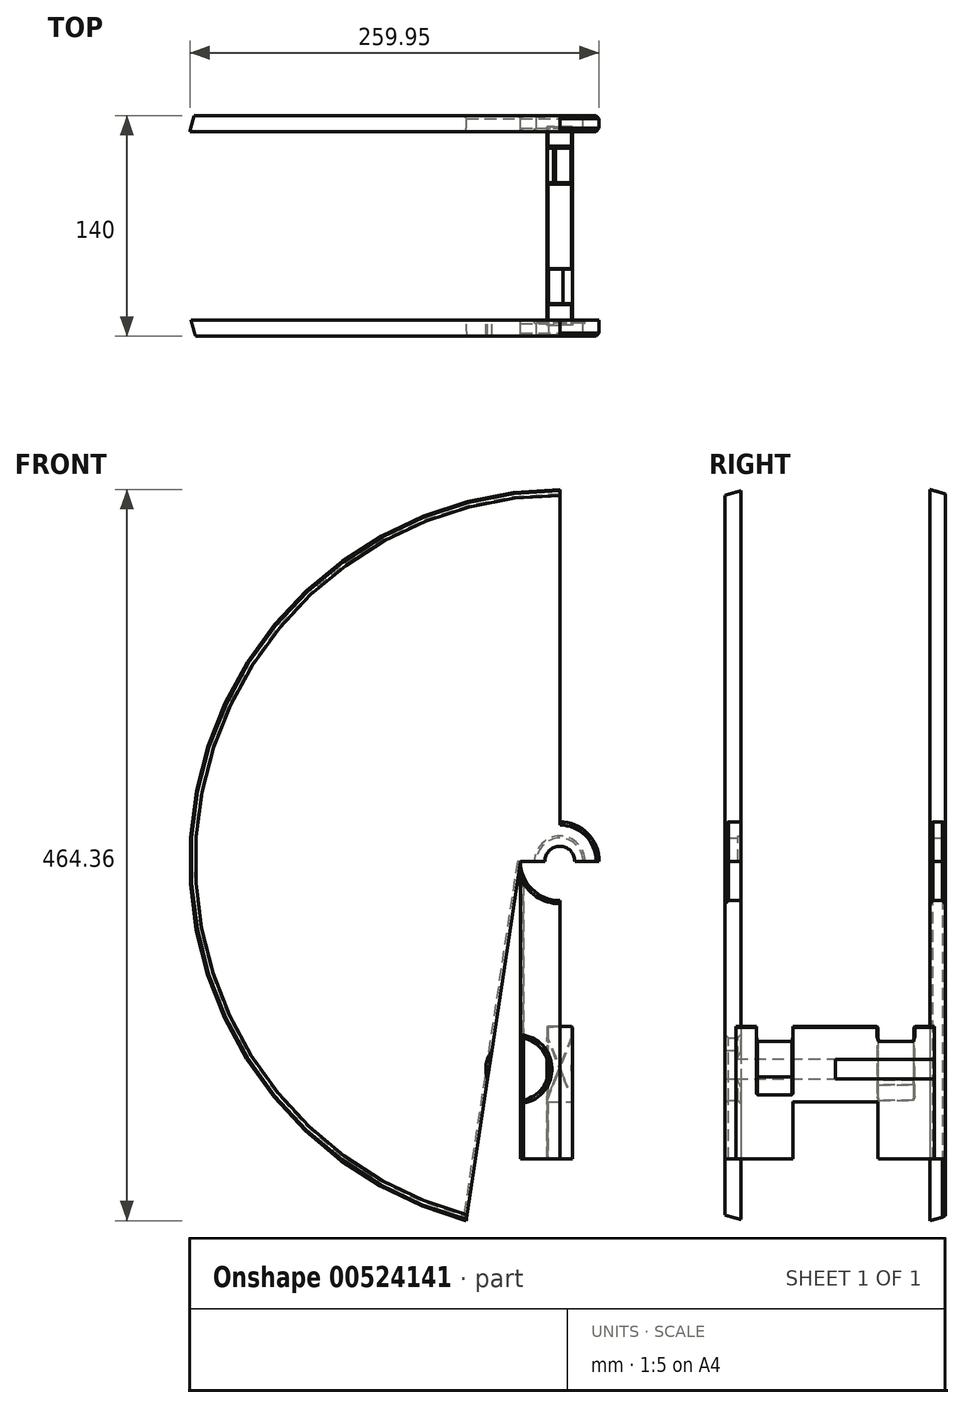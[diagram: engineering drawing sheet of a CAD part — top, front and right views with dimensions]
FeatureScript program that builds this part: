
annotation { "Feature Type Name" : "Feature", "Feature Type Description" : "" }
export const myFeature = defineFeature(function(context is Context, id is Id, definition is map)
    precondition{}
    {
        {
            var Q0;
            Q0=qCreatedBy(makeId("Right.planeOp"),FACE);
            var sketch = newSketch(context, id + "F0", { "sketchPlane" : qUnion([Q0])});
            skCircle(sketch, "E0", {"center": v(0, 0) * mm, "radius": 243.58 * mm});
            skLineSegment(sketch, "E1", {"start": v(1.44, 243.58) * mm, "end": v(1.44, -243.58) * mm});
            skCircle(sketch, "E2", {"center": v(0, 0) * mm, "radius": 251.5 * mm});
            skLineSegment(sketch, "E3", {"start": v(1.44, 243.58) * mm, "end": v(1.44, -357.35) * mm});
            skLineSegment(sketch, "E4", {"start": v(1.44, -357.35) * mm, "end": v(1.44, 517.62) * mm});
            skSolve(sketch);
        }
        {
            var Q0;
            Q0=qCreatedBy(makeId("Top.planeOp"),FACE);
            var sketch = newSketch(context, id + "F1", { "sketchPlane" : qUnion([Q0])});
            skCircle(sketch, "E5", {"center": v(0, 0) * mm, "radius": 243.58 * mm});
            skCircle(sketch, "E6", {"center": v(0, 0) * mm, "radius": 251.5 * mm});
            skSolve(sketch);
        }
        {
            var Q0;
            Q0=makeQuery(id+"F1.imprint","IMPRINT",FACE,{"disambiguationData":[TD([[makeQuery(id+"F1.imprint","IMPRINT",EDGE,{"derivedFrom":sQuery(id+"F1.wireOp",EDGE,"E5")}),1.0]])]});
            var sketch = newSketch(context, id + "F2", { "sketchPlane" : qUnion([Q0])});
            skCircle(sketch, "E7", {"center": v(0, 0) * mm, "radius": 50 * mm});
            skCircle(sketch, "E8", {"center": v(0, 0) * mm, "radius": 57.5 * mm});
            skSolve(sketch);
        }
        {
            var Q0;
            Q0=qCreatedBy(makeId("Front.planeOp"),FACE);
            var sketch = newSketch(context, id + "F3", { "sketchPlane" : qUnion([Q0])});
            skLineSegment(sketch, "E9.bottom", {"start": v(59.85, -25) * mm, "end": v(-59.85, -25) * mm});
            skLineSegment(sketch, "E9.top", {"start": v(59.85, 25) * mm, "end": v(-59.85, 25) * mm});
            skLineSegment(sketch, "E9.left", {"start": v(59.85, -25) * mm, "end": v(59.85, 25) * mm});
            skLineSegment(sketch, "E9.right", {"start": v(-59.85, -25) * mm, "end": v(-59.85, 25) * mm});
            skPoint(sketch, "E9.middle", {"position": v(0, 0) * mm});
            skCircle(sketch, "E10", {"center": v(0, 0) * mm, "radius": 14.75 * mm});
            skCircle(sketch, "E11", {"center": v(0, 0) * mm, "radius": 16 * mm});
            skCircle(sketch, "E12", {"center": v(0, 0) * mm, "radius": 9.5 * mm});
            skSolve(sketch);
        }
        {
            var Q0;
            Q0=qCreatedBy(makeId("Front.planeOp"),FACE);
            var sketch = newSketch(context, id + "F4", { "sketchPlane" : qUnion([Q0])});
            skCircle(sketch, "E13", {"center": v(0, 0) * mm, "radius": 25 * mm});
            skCircle(sketch, "E14", {"center": v(-1.44, -4.53) * mm, "radius": 243.58 * mm});
            skLineSegment(sketch, "E15", {"start": v(0, 239.04) * mm, "end": v(0, -248.1) * mm});
            skCircle(sketch, "E16", {"center": v(-1.44, -4.53) * mm, "radius": 251.5 * mm});
            skLineSegment(sketch, "E17", {"start": v(-25, 0) * mm, "end": v(-61.37, -240.62) * mm});
            skLineSegment(sketch, "E18.MirrorCS", {"start": v(25, 0) * mm, "end": v(61.37, -240.62) * mm});
            skLineSegment(sketch, "E19.bottom", {"start": v(-25, 0) * mm, "end": v(25, 0) * mm});
            skLineSegment(sketch, "E19.top", {"start": v(-25, -189.15) * mm, "end": v(25, -189.15) * mm});
            skLineSegment(sketch, "E19.left", {"start": v(-25, 0) * mm, "end": v(-25, -189.15) * mm});
            skLineSegment(sketch, "E19.right", {"start": v(25, 0) * mm, "end": v(25, -189.15) * mm});
            skSolve(sketch);
        }
        {
            var Q0;
            {var subQ0=sQuery(id+"F4.wireOp",EDGE,"E13");var subQ1=makeQuery(id+"F4.imprint","INTERSECT",VERTEX,{"derivedFrom":[subQ0,sQuery(id+"F4.wireOp",EDGE,"E17")]});Q0=makeQuery(id+"F4.imprint","IMPRINT",FACE,{"disambiguationData":[TD([[makeQuery(id+"F4.imprint","IMPRINT",EDGE,{"disambiguationData":[TD([[subQ1,1.0]])],"derivedFrom":subQ0}),1.0]])]});}
            var Q1;
            {var subQ0=sQuery(id+"F4.wireOp",EDGE,"E13");var subQ1=makeQuery(id+"F4.imprint","INTERSECT",VERTEX,{"derivedFrom":[subQ0,sQuery(id+"F4.wireOp",EDGE,"E18.MirrorCS")]});Q1=makeQuery(id+"F4.imprint","IMPRINT",FACE,{"disambiguationData":[TD([[makeQuery(id+"F4.imprint","IMPRINT",EDGE,{"disambiguationData":[TD([[subQ1,-1.0]])],"derivedFrom":subQ0}),1.0]])]});}
            var Q2;
            {var subQ0=sQuery(id+"F4.wireOp",EDGE,"E15");var subQ1=sQuery(id+"F4.wireOp",EDGE,"E13");var subQ2=makeQuery(id+"F4.imprint","INTERSECT",VERTEX,{"disambiguationData":[OD(1.0)],"derivedFrom":[subQ1,subQ0]});Q2=makeQuery(id+"F4.imprint","IMPRINT",FACE,{"disambiguationData":[TD([[makeQuery(id+"F4.imprint","IMPRINT",EDGE,{"disambiguationData":[TD([[subQ2,-1.0]])],"derivedFrom":subQ1}),-1.0]])]});}
            var Q3;
            {var subQ0=sQuery(id+"F4.wireOp",EDGE,"E19.left");Q3=makeQuery(id+"F4.imprint","IMPRINT",FACE,{"disambiguationData":[TD([[makeQuery(id+"F4.imprint","IMPRINT",EDGE,{"derivedFrom":subQ0}),1.0]])]});}
            var Q4;
            {var subQ0=sQuery(id+"F4.wireOp",EDGE,"E15");var subQ1=sQuery(id+"F4.wireOp",EDGE,"E13");var subQ2=makeQuery(id+"F4.imprint","INTERSECT",VERTEX,{"disambiguationData":[OD(1.0)],"derivedFrom":[subQ1,subQ0]});Q4=makeQuery(id+"F4.imprint","IMPRINT",FACE,{"disambiguationData":[TD([[makeQuery(id+"F4.imprint","IMPRINT",EDGE,{"disambiguationData":[TD([[subQ2,-1.0]])],"derivedFrom":subQ1}),1.0]])]});}
            var Q5;
            {var subQ1=sQuery(id+"F4.wireOp",EDGE,"E13");var subQ3=sQuery(id+"F4.wireOp",EDGE,"E15");var subQ4=makeQuery(id+"F4.imprint","INTERSECT",VERTEX,{"disambiguationData":[OD(1.0)],"derivedFrom":[subQ1,subQ3]});Q5=makeQuery(id+"F4.imprint","IMPRINT",FACE,{"disambiguationData":[TD([[makeQuery(id+"F4.imprint","IMPRINT",EDGE,{"disambiguationData":[TD([[subQ4,1.0]])],"derivedFrom":subQ3}),-1.0]])]});}
            extrude(context, id + "F5", {"entities" : qUnion([Q0, Q1, Q2, Q3, Q4, Q5]), "endBound" : BoundingType.SYMMETRIC, "depth" : 140 * mm, "hasSecondDirection" : true, "secondDirectionOppositeDirection" : true, "secondDirectionDepth" : 71 * mm});
        }
        {
            var Q0;
            {var subQ5=sQuery(id+"F4.wireOp",EDGE,"E13");var subQ6=makeQuery(id+"F4.imprint","INTERSECT",VERTEX,{"derivedFrom":[subQ5,sQuery(id+"F4.wireOp",EDGE,"E18.MirrorCS")]});Q0=makeQuery(id+"F4.imprint","IMPRINT",FACE,{"disambiguationData":[TD([[makeQuery(id+"F4.imprint","IMPRINT",EDGE,{"disambiguationData":[TD([[subQ6,-1.0]])],"derivedFrom":subQ5}),1.0]])]});}
            var Q1;
            {var subQ1=sQuery(id+"F4.wireOp",EDGE,"E13");var subQ3=sQuery(id+"F4.wireOp",EDGE,"E15");var subQ4=makeQuery(id+"F4.imprint","INTERSECT",VERTEX,{"disambiguationData":[OD(0.0)],"derivedFrom":[subQ1,subQ3]});Q1=makeQuery(id+"F4.imprint","IMPRINT",FACE,{"disambiguationData":[TD([[makeQuery(id+"F4.imprint","IMPRINT",EDGE,{"disambiguationData":[TD([[subQ4,-1.0]])],"derivedFrom":subQ3}),-1.0]])]});}
            var Q2;
            {var subQ1=sQuery(id+"F4.wireOp",EDGE,"E13");var subQ3=sQuery(id+"F4.wireOp",EDGE,"E15");var subQ4=makeQuery(id+"F4.imprint","INTERSECT",VERTEX,{"disambiguationData":[OD(1.0)],"derivedFrom":[subQ1,subQ3]});Q2=makeQuery(id+"F4.imprint","IMPRINT",FACE,{"disambiguationData":[TD([[makeQuery(id+"F4.imprint","IMPRINT",EDGE,{"disambiguationData":[TD([[subQ4,1.0]])],"derivedFrom":subQ3}),-1.0]])]});}
            var Q3;
            {var subQ0=sQuery(id+"F4.wireOp",EDGE,"E15");var subQ1=sQuery(id+"F4.wireOp",EDGE,"E13");var subQ2=makeQuery(id+"F4.imprint","INTERSECT",VERTEX,{"disambiguationData":[OD(1.0)],"derivedFrom":[subQ1,subQ0]});Q3=makeQuery(id+"F4.imprint","IMPRINT",FACE,{"disambiguationData":[TD([[makeQuery(id+"F4.imprint","IMPRINT",EDGE,{"disambiguationData":[TD([[subQ2,-1.0]])],"derivedFrom":subQ1}),1.0]])]});}
            var Q4;
            {var subQ0=sQuery(id+"F4.wireOp",EDGE,"E15");var subQ1=sQuery(id+"F4.wireOp",EDGE,"E13");var subQ2=makeQuery(id+"F4.imprint","INTERSECT",VERTEX,{"disambiguationData":[OD(1.0)],"derivedFrom":[subQ1,subQ0]});Q4=makeQuery(id+"F4.imprint","IMPRINT",FACE,{"disambiguationData":[TD([[makeQuery(id+"F4.imprint","IMPRINT",EDGE,{"disambiguationData":[TD([[subQ2,-1.0]])],"derivedFrom":subQ1}),-1.0]])]});}
            var Q5;
            {var subQ0=sQuery(id+"F4.wireOp",EDGE,"E19.left");Q5=makeQuery(id+"F4.imprint","IMPRINT",FACE,{"disambiguationData":[TD([[makeQuery(id+"F4.imprint","IMPRINT",EDGE,{"derivedFrom":subQ0}),1.0]])]});}
            extrude(context, id + "F6", {"entities" : qUnion([Q0, Q1, Q2, Q3, Q4, Q5]), "operationType" : NewBodyOperationType.REMOVE, "endBound" : BoundingType.SYMMETRIC, "oppositeDirection" : true, "depth" : 120 * mm});
        }
        {
            var Q0;
            {var subQ0=sQuery(id+"F0.wireOp",EDGE,"E4");var subQ1=sQuery(id+"F0.wireOp",EDGE,"E0");var subQ2=makeQuery(id+"F0.imprint","INTERSECT",VERTEX,{"disambiguationData":[OD(0.0)],"derivedFrom":[subQ1,subQ0]});Q0=makeQuery(id+"F0.imprint","IMPRINT",FACE,{"disambiguationData":[TD([[makeQuery(id+"F0.imprint","IMPRINT",EDGE,{"disambiguationData":[TD([[subQ2,1.0]])],"derivedFrom":subQ1}),1.0]])]});}
            var Q1;
            Q1=sQuery(id+"F0.wireOp",EDGE,"E4");
            revolve(context, id + "F7", {"operationType" : NewBodyOperationType.INTERSECT, "entities" : qUnion([Q0]), "axis" : qUnion([Q1]), "revolveType" : RevolveType.FULL});
        }
        {
            var Q0;
            Q0=makeQuery(id+"F3.imprint","IMPRINT",FACE,{"disambiguationData":[TD([[makeQuery(id+"F3.imprint","IMPRINT",EDGE,{"derivedFrom":sQuery(id+"F3.wireOp",EDGE,"E10")}),1.0]])]});
            var Q1;
            Q1=makeQuery(id+"F3.imprint","IMPRINT",FACE,{"disambiguationData":[TD([[makeQuery(id+"F3.imprint","IMPRINT",EDGE,{"derivedFrom":sQuery(id+"F3.wireOp",EDGE,"E10")}),-1.0]])]});
            var Q2;
            Q2=sQuery(id+"F4.wireOp",EDGE,"E13");
            extrude(context, id + "F8", {"entities" : qUnion([Q0, Q1]), "operationType" : NewBodyOperationType.REMOVE, "surfaceEntities" : qUnion([Q2]), "endBound" : BoundingType.SYMMETRIC, "depth" : 123.5 * mm});
        }
        {
            var Q0;
            Q0=makeQuery(id+"F3.imprint","IMPRINT",FACE,{"disambiguationData":[TD([[makeQuery(id+"F3.imprint","IMPRINT",EDGE,{"derivedFrom":sQuery(id+"F3.wireOp",EDGE,"E10")}),1.0]])]});
            extrude(context, id + "F9", {"entities" : qUnion([Q0]), "operationType" : NewBodyOperationType.REMOVE, "endBound" : BoundingType.SYMMETRIC, "depth" : 139 * mm});
        }
        {
            var Q0;
            Q0=qCreatedBy(makeId("Front.planeOp"),FACE);
            var sketch = newSketch(context, id + "F10", { "sketchPlane" : qUnion([Q0])});
            skLineSegment(sketch, "E20.bottom", {"start": v(-62.5, 105) * mm, "end": v(62.5, 105) * mm, "construction": true});
            skLineSegment(sketch, "E20.top", {"start": v(-62.5, -105) * mm, "end": v(62.5, -105) * mm, "construction": true});
            skLineSegment(sketch, "E20.left", {"start": v(-62.5, 105) * mm, "end": v(-62.5, -105) * mm, "construction": true});
            skLineSegment(sketch, "E20.right", {"start": v(62.5, 105) * mm, "end": v(62.5, -105) * mm, "construction": true});
            skPoint(sketch, "E20.middle", {"position": v(0, 0) * mm});
            skLineSegment(sketch, "E21", {"start": v(0, 0) * mm, "end": v(0, -232.3) * mm, "construction": true});
            skPoint(sketch, "E22.firstSnap0", {"position": v(0, -105) * mm});
            skLineSegment(sketch, "E22.bottom", {"start": v(0, -105) * mm, "end": v(-8.15, -105) * mm});
            skLineSegment(sketch, "E22.top", {"start": v(0, -232.3) * mm, "end": v(-8.15, -232.3) * mm});
            skLineSegment(sketch, "E22.left", {"start": v(0, -105) * mm, "end": v(0, -232.3) * mm});
            skLineSegment(sketch, "E22.right", {"start": v(-8.15, -105) * mm, "end": v(-8.15, -232.3) * mm});
            skLineSegment(sketch, "E23.bottom", {"start": v(0, -105) * mm, "end": v(8.15, -105) * mm});
            skLineSegment(sketch, "E23.top", {"start": v(0, -232.3) * mm, "end": v(8.15, -232.3) * mm});
            skLineSegment(sketch, "E23.right", {"start": v(8.15, -105) * mm, "end": v(8.15, -232.3) * mm});
            skSolve(sketch);
        }
        {
            var Q0;
            Q0=makeQuery(id+"F3.imprint","IMPRINT",FACE,{"disambiguationData":[TD([[makeQuery(id+"F3.imprint","IMPRINT",EDGE,{"derivedFrom":sQuery(id+"F3.wireOp",EDGE,"E12")}),1.0]])]});
            var Q1;
            Q1=sQuery(id+"F3.wireOp",EDGE,"E12");
            extrude(context, id + "F11", {"entities" : qUnion([Q0]), "operationType" : NewBodyOperationType.REMOVE, "surfaceEntities" : qUnion([Q1]), "endBound" : BoundingType.SYMMETRIC, "oppositeDirection" : true, "depth" : 200 * mm});
        }
        {
            var Q0;
            Q0=makeQuery(id+"F10.imprint","IMPRINT",FACE,{"disambiguationData":[TD([[makeQuery(id+"F10.imprint","IMPRINT",EDGE,{"derivedFrom":sQuery(id+"F10.wireOp",EDGE,"E23.bottom")}),-1.0]])]});
            var Q1;
            Q1=makeQuery(id+"F10.imprint","IMPRINT",FACE,{"disambiguationData":[TD([[makeQuery(id+"F10.imprint","IMPRINT",EDGE,{"derivedFrom":sQuery(id+"F10.wireOp",EDGE,"E22.bottom")}),1.0]])]});
            extrude(context, id + "F12", {"entities" : qUnion([Q0, Q1]), "operationType" : NewBodyOperationType.REMOVE, "endBound" : BoundingType.SYMMETRIC, "oppositeDirection" : true, "depth" : 126 * mm});
        }
        {
            var Q0;
            Q0=qCreatedBy(makeId("Front.planeOp"),FACE);
            var sketch = newSketch(context, id + "F13", { "sketchPlane" : qUnion([Q0])});
            skLineSegment(sketch, "E24.bottom", {"start": v(-62.5, 105) * mm, "end": v(62.5, 105) * mm, "construction": true});
            skLineSegment(sketch, "E24.top", {"start": v(-62.5, -105) * mm, "end": v(62.5, -105) * mm, "construction": true});
            skLineSegment(sketch, "E24.left", {"start": v(-62.5, 105) * mm, "end": v(-62.5, -105) * mm, "construction": true});
            skLineSegment(sketch, "E24.right", {"start": v(62.5, 105) * mm, "end": v(62.5, -105) * mm, "construction": true});
            skPoint(sketch, "E24.middle", {"position": v(0, 0) * mm});
            skLineSegment(sketch, "E25", {"start": v(0, 0) * mm, "end": v(0, -189) * mm, "construction": true});
            skPoint(sketch, "E26.firstSnap0", {"position": v(0, -105) * mm});
            skLineSegment(sketch, "E26.bottom", {"start": v(0, -105) * mm, "end": v(-8, -105) * mm});
            skLineSegment(sketch, "E26.top", {"start": v(0, -189) * mm, "end": v(-8, -189) * mm});
            skLineSegment(sketch, "E26.left", {"start": v(0, -105) * mm, "end": v(0, -189) * mm});
            skLineSegment(sketch, "E26.right", {"start": v(-8, -105) * mm, "end": v(-8, -189) * mm});
            skLineSegment(sketch, "E27.bottom", {"start": v(0, -105) * mm, "end": v(8, -105) * mm});
            skLineSegment(sketch, "E27.top", {"start": v(0, -189) * mm, "end": v(8, -189) * mm});
            skLineSegment(sketch, "E27.right", {"start": v(8, -105) * mm, "end": v(8, -189) * mm});
            skLineSegment(sketch, "E28", {"start": v(-63.01, -125.52) * mm, "end": v(62.14, -125.52) * mm, "construction": true});
            skLineSegment(sketch, "E29.bottom", {"start": v(-56.15, -105) * mm, "end": v(-48.17, -105) * mm});
            skSolve(sketch);
        }
        {
            var Q0;
            Q0=qCreatedBy(makeId("Front.planeOp"),FACE);
            var sketch = newSketch(context, id + "F14", { "sketchPlane" : qUnion([Q0])});
            skLineSegment(sketch, "E30", {"start": v(-75.64, -132) * mm, "end": v(82.36, -132) * mm, "construction": true});
            skCircle(sketch, "E31", {"center": v(-26.97, -132) * mm, "radius": 20 * mm});
            skCircle(sketch, "E32", {"center": v(27.03, -132) * mm, "radius": 20 * mm});
            skLineSegment(sketch, "E33", {"start": v(0, -132) * mm, "end": v(0, 0) * mm, "construction": true});
            skSolve(sketch);
        }
        {
            var Q0;
            Q0=makeQuery(id+"F13.imprint","IMPRINT",FACE,{"disambiguationData":[TD([[makeQuery(id+"F13.imprint","IMPRINT",EDGE,{"derivedFrom":sQuery(id+"F13.wireOp",EDGE,"E26.bottom")}),1.0]])]});
            var Q1;
            Q1=makeQuery(id+"F13.imprint","IMPRINT",FACE,{"disambiguationData":[TD([[makeQuery(id+"F13.imprint","IMPRINT",EDGE,{"derivedFrom":sQuery(id+"F13.wireOp",EDGE,"E27.bottom")}),-1.0]])]});
            extrude(context, id + "F15", {"entities" : qUnion([Q0, Q1]), "endBound" : BoundingType.SYMMETRIC, "depth" : 126 * mm});
        }
        {
            var Q0;
            Q0=makeQuery(id+"F14.imprint","IMPRINT",FACE,{"disambiguationData":[TD([[makeQuery(id+"F14.imprint","IMPRINT",EDGE,{"derivedFrom":sQuery(id+"F14.wireOp",EDGE,"E32")}),1.0]])]});
            extrude(context, id + "F16", {"entities" : qUnion([Q0]), "operationType" : NewBodyOperationType.REMOVE, "oppositeDirection" : true, "depth" : 125.4 * mm});
        }
        {
            var Q0;
            Q0=makeQuery(id+"F14.imprint","IMPRINT",FACE,{"disambiguationData":[TD([[makeQuery(id+"F14.imprint","IMPRINT",EDGE,{"derivedFrom":sQuery(id+"F14.wireOp",EDGE,"E31")}),1.0]])]});
            extrude(context, id + "F17", {"entities" : qUnion([Q0]), "operationType" : NewBodyOperationType.REMOVE, "depth" : 97.5 * mm});
        }
        {
            var Q0;
            Q0=qCreatedBy(makeId("Front.planeOp"),FACE);
            var sketch = newSketch(context, id + "F18", { "sketchPlane" : qUnion([Q0])});
            skCircle(sketch, "E34", {"center": v(0, 0) * mm, "radius": 242.5 * mm});
            skSolve(sketch);
        }
        {
            var Q0;
            Q0=makeQuery(id+"F14.imprint","IMPRINT",FACE,{"disambiguationData":[TD([[makeQuery(id+"F14.imprint","IMPRINT",EDGE,{"derivedFrom":sQuery(id+"F14.wireOp",EDGE,"E31")}),1.0]])]});
            extrude(context, id + "F19", {"entities" : qUnion([Q0]), "operationType" : NewBodyOperationType.REMOVE, "depth" : 159.82 * mm, "hasSecondDirection" : true, "secondDirectionOppositeDirection" : false, "secondDirectionDepth" : 5 * mm});
        }
        {
            var Q0;
            Q0=makeQuery(id+"F14.imprint","IMPRINT",FACE,{"disambiguationData":[TD([[makeQuery(id+"F14.imprint","IMPRINT",EDGE,{"derivedFrom":sQuery(id+"F14.wireOp",EDGE,"E32")}),1.0]])]});
            extrude(context, id + "F20", {"entities" : qUnion([Q0]), "operationType" : NewBodyOperationType.REMOVE, "oppositeDirection" : true, "depth" : 139.38 * mm, "hasSecondDirection" : true, "secondDirectionOppositeDirection" : true, "secondDirectionDepth" : 5 * mm});
        }
        {
            var Q0;
            Q0=qSketchRegion(id+"F14",true);
            var sketch = newSketch(context, id + "F21", { "sketchPlane" : qUnion([Q0])});
            skLineSegment(sketch, "E35", {"start": v(-64.6, -131.33) * mm, "end": v(93.4, -131.33) * mm, "construction": true});
            skCircle(sketch, "E36", {"center": v(-26.64, -131.33) * mm, "radius": 25 * mm});
            skCircle(sketch, "E37", {"center": v(26.36, -131.33) * mm, "radius": 25 * mm});
            skLineSegment(sketch, "E38", {"start": v(0, -131.33) * mm, "end": v(0, 0.67) * mm, "construction": true});
            skSolve(sketch);
        }
        {
            var Q0;
            Q0=qSketchRegion(id+"F21",true);
            var sketch = newSketch(context, id + "F22", { "sketchPlane" : qUnion([Q0])});
            skLineSegment(sketch, "E39.bottom", {"start": v(-20, -81.91) * mm, "end": v(20, -81.91) * mm});
            skLineSegment(sketch, "E39.top", {"start": v(-20, -181.91) * mm, "end": v(20, -181.91) * mm});
            skLineSegment(sketch, "E39.left", {"start": v(-20, -81.91) * mm, "end": v(-20, -181.91) * mm});
            skLineSegment(sketch, "E39.right", {"start": v(20, -81.91) * mm, "end": v(20, -181.91) * mm});
            skPoint(sketch, "E39.middle", {"position": v(0, -131.91) * mm});
            skLineSegment(sketch, "E40", {"start": v(20, -181.91) * mm, "end": v(-20, -81.91) * mm});
            skLineSegment(sketch, "E41", {"start": v(20, -81.91) * mm, "end": v(-20, -181.91) * mm});
            skSolve(sketch);
        }
        {
            var Q0;
            {var subQ0=sQuery(id+"F22.wireOp",EDGE,"E39.left");var subQ1=makeQuery(id+"F21.imprint","IMPRINT",EDGE,{"derivedFrom":sQuery(id+"F21.wireOp",EDGE,"E36")});var subQ2=makeQuery(id+"F22.imprint","INTERSECT",VERTEX,{"disambiguationData":[OD(0.0)],"derivedFrom":[subQ1,subQ0]});Q0=makeQuery(id+"F22.imprint","IMPRINT",FACE,{"disambiguationData":[TD([[makeQuery(id+"F22.imprint","IMPRINT",EDGE,{"disambiguationData":[TD([[subQ2,-1.0]])],"derivedFrom":subQ0}),-1.0]])]});}
            var Q1;
            Q1=makeQuery(id+"F21.imprint","IMPRINT",FACE,{"disambiguationData":[TD([[makeQuery(id+"F21.imprint","IMPRINT",EDGE,{"derivedFrom":sQuery(id+"F21.wireOp",EDGE,"E36")}),1.0]])]});
            var Q2;
            Q2=makeQuery(id+"F21.imprint","IMPRINT",FACE,{"disambiguationData":[TD([[makeQuery(id+"F21.imprint","IMPRINT",EDGE,{"derivedFrom":makeQuery(id+"F14.imprint","IMPRINT",EDGE,{"derivedFrom":sQuery(id+"F14.wireOp",EDGE,"E31")})}),1.0]])]});
            var Q3;
            {var subQ1=sQuery(id+"F22.wireOp",EDGE,"E39.left");var subQ3=makeQuery(id+"F21.imprint","IMPRINT",EDGE,{"derivedFrom":sQuery(id+"F21.wireOp",EDGE,"E36")});var subQ4=makeQuery(id+"F22.imprint","INTERSECT",VERTEX,{"disambiguationData":[OD(0.0)],"derivedFrom":[subQ3,subQ1]});Q3=makeQuery(id+"F22.imprint","IMPRINT",FACE,{"disambiguationData":[TD([[makeQuery(id+"F22.imprint","IMPRINT",EDGE,{"disambiguationData":[TD([[subQ4,1.0]])],"derivedFrom":subQ3}),-1.0]])]});}
            var Q4;
            {var subQ1=sQuery(id+"F22.wireOp",EDGE,"E39.bottom");Q4=makeQuery(id+"F22.imprint","IMPRINT",FACE,{"disambiguationData":[TD([[makeQuery(id+"F22.imprint","IMPRINT",EDGE,{"derivedFrom":subQ1}),-1.0]])]});}
            var Q5;
            {var subQ0=sQuery(id+"F22.wireOp",EDGE,"E41");var subQ1=sQuery(id+"F22.wireOp",EDGE,"E40");var subQ2=makeQuery(id+"F22.imprint","INTERSECT",VERTEX,{"derivedFrom":[subQ1,subQ0]});Q5=makeQuery(id+"F22.imprint","IMPRINT",FACE,{"disambiguationData":[TD([[makeQuery(id+"F22.imprint","IMPRINT",EDGE,{"disambiguationData":[TD([[subQ2,-1.0]])],"derivedFrom":subQ1}),1.0]])]});}
            var Q6;
            {var subQ0=sQuery(id+"F22.wireOp",EDGE,"E41");var subQ1=makeQuery(id+"F21.imprint","IMPRINT",EDGE,{"derivedFrom":sQuery(id+"F21.wireOp",EDGE,"E37")});var subQ2=makeQuery(id+"F22.imprint","INTERSECT",VERTEX,{"disambiguationData":[OD(0.0)],"derivedFrom":[subQ1,subQ0]});Q6=makeQuery(id+"F22.imprint","IMPRINT",FACE,{"disambiguationData":[TD([[makeQuery(id+"F22.imprint","IMPRINT",EDGE,{"disambiguationData":[TD([[subQ2,-1.0]])],"derivedFrom":subQ0}),-1.0]])]});}
            extrude(context, id + "F23", {"entities" : qUnion([Q0, Q1, Q2, Q3, Q4, Q5, Q6]), "operationType" : NewBodyOperationType.REMOVE, "oppositeDirection" : true, "depth" : 50 * mm, "hasSecondDirection" : true, "secondDirectionOppositeDirection" : true, "secondDirectionDepth" : 27 * mm});
        }
        {
            var Q0;
            {var subQ0=sQuery(id+"F22.wireOp",EDGE,"E39.right");var subQ1=makeQuery(id+"F21.imprint","IMPRINT",EDGE,{"derivedFrom":makeQuery(id+"F14.imprint","IMPRINT",EDGE,{"derivedFrom":sQuery(id+"F14.wireOp",EDGE,"E32")})});var subQ2=makeQuery(id+"F22.imprint","INTERSECT",VERTEX,{"disambiguationData":[OD(0.0)],"derivedFrom":[subQ1,subQ0]});Q0=makeQuery(id+"F22.imprint","IMPRINT",FACE,{"disambiguationData":[TD([[makeQuery(id+"F22.imprint","IMPRINT",EDGE,{"disambiguationData":[TD([[subQ2,-1.0]])],"derivedFrom":subQ0}),-1.0]])]});}
            var Q1;
            {var subQ1=makeQuery(id+"F21.imprint","IMPRINT",EDGE,{"derivedFrom":sQuery(id+"F21.wireOp",EDGE,"E37")});var subQ4=sQuery(id+"F22.wireOp",EDGE,"E39.right");var subQ5=makeQuery(id+"F22.imprint","INTERSECT",VERTEX,{"disambiguationData":[OD(0.0)],"derivedFrom":[subQ1,subQ4]});Q1=makeQuery(id+"F22.imprint","IMPRINT",FACE,{"disambiguationData":[TD([[makeQuery(id+"F22.imprint","IMPRINT",EDGE,{"disambiguationData":[TD([[subQ5,-1.0]])],"derivedFrom":subQ4}),-1.0]])]});}
            var Q2;
            Q2=makeQuery(id+"F21.imprint","IMPRINT",FACE,{"disambiguationData":[TD([[makeQuery(id+"F21.imprint","IMPRINT",EDGE,{"derivedFrom":makeQuery(id+"F14.imprint","IMPRINT",EDGE,{"derivedFrom":sQuery(id+"F14.wireOp",EDGE,"E32")})}),1.0]])]});
            var Q3;
            {var subQ0=sQuery(id+"F22.wireOp",EDGE,"E41");var subQ1=sQuery(id+"F22.wireOp",EDGE,"E40");var subQ2=makeQuery(id+"F22.imprint","INTERSECT",VERTEX,{"derivedFrom":[subQ1,subQ0]});Q3=makeQuery(id+"F22.imprint","IMPRINT",FACE,{"disambiguationData":[TD([[makeQuery(id+"F22.imprint","IMPRINT",EDGE,{"disambiguationData":[TD([[subQ2,1.0]])],"derivedFrom":subQ1}),-1.0]])]});}
            var Q4;
            {var subQ1=sQuery(id+"F22.wireOp",EDGE,"E39.right");var subQ3=makeQuery(id+"F21.imprint","IMPRINT",EDGE,{"derivedFrom":sQuery(id+"F21.wireOp",EDGE,"E37")});var subQ4=makeQuery(id+"F22.imprint","INTERSECT",VERTEX,{"disambiguationData":[OD(0.0)],"derivedFrom":[subQ3,subQ1]});Q4=makeQuery(id+"F22.imprint","IMPRINT",FACE,{"disambiguationData":[TD([[makeQuery(id+"F22.imprint","IMPRINT",EDGE,{"disambiguationData":[TD([[subQ4,-1.0]])],"derivedFrom":subQ3}),-1.0]])]});}
            var Q5;
            {var subQ1=sQuery(id+"F22.wireOp",EDGE,"E39.bottom");Q5=makeQuery(id+"F22.imprint","IMPRINT",FACE,{"disambiguationData":[TD([[makeQuery(id+"F22.imprint","IMPRINT",EDGE,{"derivedFrom":subQ1}),-1.0]])]});}
            var Q6;
            Q6=makeQuery(id+"F21.imprint","IMPRINT",FACE,{"disambiguationData":[TD([[makeQuery(id+"F21.imprint","IMPRINT",EDGE,{"derivedFrom":sQuery(id+"F21.wireOp",EDGE,"E37")}),1.0]])]});
            var Q7;
            {var subQ0=sQuery(id+"F22.wireOp",EDGE,"E40");var subQ1=makeQuery(id+"F21.imprint","IMPRINT",EDGE,{"derivedFrom":sQuery(id+"F21.wireOp",EDGE,"E36")});var subQ2=makeQuery(id+"F22.imprint","INTERSECT",VERTEX,{"disambiguationData":[OD(0.0)],"derivedFrom":[subQ1,subQ0]});Q7=makeQuery(id+"F22.imprint","IMPRINT",FACE,{"disambiguationData":[TD([[makeQuery(id+"F22.imprint","IMPRINT",EDGE,{"disambiguationData":[TD([[subQ2,-1.0]])],"derivedFrom":subQ0}),-1.0]])]});}
            extrude(context, id + "F24", {"entities" : qUnion([Q0, Q1, Q2, Q3, Q4, Q5, Q6, Q7]), "operationType" : NewBodyOperationType.REMOVE, "depth" : 50 * mm, "hasSecondDirection" : true, "secondDirectionOppositeDirection" : false, "secondDirectionDepth" : 27 * mm});
        }
        {
            var Q0;
            Q0=makeQuery(id+"F5.opExtrude","CAP_EDGE",EDGE,{"disambiguationData":[OSD([sQuery(id+"F4.wireOp",EDGE,"E17")])],"isStart":true});
            var Q1;
            Q1=makeQuery(id+"F5.opExtrude","CAP_EDGE",EDGE,{"disambiguationData":[OSD([sQuery(id+"F4.wireOp",EDGE,"E18.MirrorCS")])],"isStart":true});
            var Q2;
            Q2=makeQuery(id+"F5.opExtrude","CAP_EDGE",EDGE,{"disambiguationData":[OSD([sQuery(id+"F4.wireOp",EDGE,"E19.right")])],"isStart":false});
            var Q3;
            Q3=makeQuery(id+"F5.opExtrude","CAP_EDGE",EDGE,{"disambiguationData":[OSD([sQuery(id+"F4.wireOp",EDGE,"E13")])],"isStart":false});
            var Q4;
            Q4=makeQuery(id+"F5.opExtrude","CAP_EDGE",EDGE,{"disambiguationData":[OSD([sQuery(id+"F4.wireOp",EDGE,"E13")])],"isStart":true});
            var Q5;
            Q5=makeQuery(id+"F5.opExtrude","CAP_EDGE",EDGE,{"disambiguationData":[OSD([sQuery(id+"F4.wireOp",EDGE,"E19.left")])],"isStart":true});
            var Q6;
            Q6=makeQuery(id+"F5.opExtrude","CAP_EDGE",EDGE,{"disambiguationData":[OSD([sQuery(id+"F4.wireOp",EDGE,"E19.right")])],"isStart":true});
            var Q7;
            Q7=makeQuery(id+"F17.boolean.opBoolean","INTERSECT",EDGE,{"derivedFrom":[makeQuery(id+"F5.opExtrude","CAP_FACE",FACE,{"disambiguationData":[OSD([sQuery(id+"F4.wireOp",EDGE,"E13"),sQuery(id+"F4.wireOp",EDGE,"E19.top"),sQuery(id+"F4.wireOp",EDGE,"E19.left"),sQuery(id+"F4.wireOp",EDGE,"E19.right")])],"isStart":false}),makeQuery(id+"F17.opExtrude","SWEPT_FACE",FACE,{"disambiguationData":[OSD([sQuery(id+"F14.wireOp",EDGE,"E31")])]})]});
            var Q8;
            Q8=makeQuery(id+"F16.boolean.opBoolean","INTERSECT",EDGE,{"derivedFrom":[makeQuery(id+"F5.opExtrude","CAP_FACE",FACE,{"disambiguationData":[OSD([sQuery(id+"F4.wireOp",EDGE,"E13"),sQuery(id+"F4.wireOp",EDGE,"E19.top"),sQuery(id+"F4.wireOp",EDGE,"E19.left"),sQuery(id+"F4.wireOp",EDGE,"E19.right")])],"isStart":true}),makeQuery(id+"F16.opExtrude","SWEPT_FACE",FACE,{"disambiguationData":[OSD([sQuery(id+"F14.wireOp",EDGE,"E32")])]})]});
            var Q9;
            {var subQ0=sQuery(id+"F4.wireOp",EDGE,"E19.left");var subQ1=sQuery(id+"F4.wireOp",EDGE,"E19.top");Q9=makeQuery(id+"F17.boolean.opBoolean","SPLIT",EDGE,{"disambiguationData":[TD([makeQuery(id+"F5.opExtrude","SWEPT_FACE",FACE,{"disambiguationData":[OSD([subQ1])]})])],"derivedFrom":makeQuery(id+"F5.opExtrude","CAP_EDGE",EDGE,{"disambiguationData":[OSD([subQ0])],"isStart":false})});}
            var Q10;
            Q10=makeQuery(id+"F6.boolean.opBoolean","COPY",EDGE,{"derivedFrom":makeQuery(id+"F6.opExtrude","CAP_EDGE",EDGE,{"disambiguationData":[OSD([sQuery(id+"F4.wireOp",EDGE,"E19.right")])],"isStart":true})});
            var Q11;
            Q11=makeQuery(id+"F6.boolean.opBoolean","COPY",EDGE,{"derivedFrom":makeQuery(id+"F6.opExtrude","CAP_EDGE",EDGE,{"disambiguationData":[OSD([sQuery(id+"F4.wireOp",EDGE,"E13")])],"isStart":true})});
            var Q12;
            Q12=makeQuery(id+"F6.boolean.opBoolean","COPY",EDGE,{"derivedFrom":makeQuery(id+"F6.opExtrude","CAP_EDGE",EDGE,{"disambiguationData":[OSD([sQuery(id+"F4.wireOp",EDGE,"E19.left")])],"isStart":false})});
            var Q13;
            Q13=makeQuery(id+"F6.boolean.opBoolean","COPY",EDGE,{"derivedFrom":makeQuery(id+"F6.opExtrude","CAP_EDGE",EDGE,{"disambiguationData":[OSD([sQuery(id+"F4.wireOp",EDGE,"E13")])],"isStart":false})});
            var Q14;
            {var subQ0=sQuery(id+"F4.wireOp",EDGE,"E13");var subQ1=sQuery(id+"F4.wireOp",EDGE,"E19.right");Q14=makeQuery(id+"F16.boolean.opBoolean","SPLIT",EDGE,{"disambiguationData":[TD([makeQuery(id+"F5.opExtrude","SWEPT_FACE",FACE,{"disambiguationData":[OSD([subQ0])]})])],"derivedFrom":makeQuery(id+"F6.boolean.opBoolean","COPY",EDGE,{"derivedFrom":makeQuery(id+"F6.opExtrude","CAP_EDGE",EDGE,{"disambiguationData":[OSD([subQ1])],"isStart":false})})});}
            var Q15;
            {var subQ0=sQuery(id+"F4.wireOp",EDGE,"E19.top");var subQ1=sQuery(id+"F4.wireOp",EDGE,"E19.right");Q15=makeQuery(id+"F16.boolean.opBoolean","SPLIT",EDGE,{"disambiguationData":[TD([makeQuery(id+"F5.opExtrude","SWEPT_FACE",FACE,{"disambiguationData":[OSD([subQ0])]})])],"derivedFrom":makeQuery(id+"F6.boolean.opBoolean","COPY",EDGE,{"derivedFrom":makeQuery(id+"F6.opExtrude","CAP_EDGE",EDGE,{"disambiguationData":[OSD([subQ1])],"isStart":false})})});}
            var Q16;
            {var subQ0=sQuery(id+"F4.wireOp",EDGE,"E19.left");var subQ1=sQuery(id+"F4.wireOp",EDGE,"E19.top");var subQ2=sQuery(id+"F4.wireOp",EDGE,"E19.right");var subQ3=sQuery(id+"F4.wireOp",EDGE,"E13");Q16=makeQuery(id+"F16.boolean.opBoolean","INTERSECT",EDGE,{"disambiguationData":[OD(1.0)],"derivedFrom":[makeQuery(id+"F8.boolean.opBoolean","SPLIT",FACE,{"disambiguationData":[TD([makeQuery(id+"F5.opExtrude","SWEPT_FACE",FACE,{"disambiguationData":[OSD([subQ3])]})])],"derivedFrom":makeQuery(id+"F6.boolean.opBoolean","COPY",FACE,{"derivedFrom":makeQuery(id+"F6.opExtrude","CAP_FACE",FACE,{"disambiguationData":[OSD([subQ3,subQ1,subQ0,subQ2])],"isStart":false})})}),makeQuery(id+"F16.opExtrude","SWEPT_FACE",FACE,{"disambiguationData":[OSD([sQuery(id+"F14.wireOp",EDGE,"E32")])]})]});}
            var Q17;
            {var subQ0=sQuery(id+"F4.wireOp",EDGE,"E19.left");var subQ1=sQuery(id+"F4.wireOp",EDGE,"E19.top");var subQ2=sQuery(id+"F4.wireOp",EDGE,"E19.right");var subQ3=sQuery(id+"F4.wireOp",EDGE,"E13");Q17=makeQuery(id+"F16.boolean.opBoolean","INTERSECT",EDGE,{"disambiguationData":[OD(0.0)],"derivedFrom":[makeQuery(id+"F8.boolean.opBoolean","SPLIT",FACE,{"disambiguationData":[TD([makeQuery(id+"F5.opExtrude","SWEPT_FACE",FACE,{"disambiguationData":[OSD([subQ3])]})])],"derivedFrom":makeQuery(id+"F6.boolean.opBoolean","COPY",FACE,{"derivedFrom":makeQuery(id+"F6.opExtrude","CAP_FACE",FACE,{"disambiguationData":[OSD([subQ3,subQ1,subQ0,subQ2])],"isStart":false})})}),makeQuery(id+"F16.opExtrude","SWEPT_FACE",FACE,{"disambiguationData":[OSD([sQuery(id+"F14.wireOp",EDGE,"E32")])]})]});}
            var Q18;
            Q18=makeQuery(id+"F16.boolean.opBoolean","INTERSECT",EDGE,{"derivedFrom":[makeQuery(id+"F12.boolean.opBoolean","COPY",FACE,{"derivedFrom":makeQuery(id+"F12.opExtrude","CAP_FACE",FACE,{"disambiguationData":[OSD([sQuery(id+"F10.wireOp",EDGE,"E22.bottom"),sQuery(id+"F10.wireOp",EDGE,"E22.top"),sQuery(id+"F10.wireOp",EDGE,"E22.right"),sQuery(id+"F10.wireOp",EDGE,"E23.bottom"),sQuery(id+"F10.wireOp",EDGE,"E23.top"),sQuery(id+"F10.wireOp",EDGE,"E23.right")])],"isStart":false})}),makeQuery(id+"F16.opExtrude","SWEPT_FACE",FACE,{"disambiguationData":[OSD([sQuery(id+"F14.wireOp",EDGE,"E32")])]})]});
            var Q19;
            Q19=makeQuery(id+"F20.boolean.opBoolean","INTERSECT",EDGE,{"derivedFrom":[makeQuery(id+"F15.opExtrude","SWEPT_FACE",FACE,{"disambiguationData":[OSD([sQuery(id+"F13.wireOp",EDGE,"E27.right")])]}),makeQuery(id+"F20.opExtrude","CAP_FACE",FACE,{"disambiguationData":[OSD([sQuery(id+"F14.wireOp",EDGE,"E32")])],"isStart":true})]});
            var Q20;
            Q20=makeQuery(id+"F19.boolean.opBoolean","COPY",EDGE,{"derivedFrom":makeQuery(id+"F19.opExtrude","CAP_EDGE",EDGE,{"disambiguationData":[OSD([sQuery(id+"F14.wireOp",EDGE,"E31")])],"isStart":true})});
            var Q21;
            Q21=makeQuery(id+"F19.boolean.opBoolean","INTERSECT",EDGE,{"derivedFrom":[makeQuery(id+"F15.opExtrude","CAP_FACE",FACE,{"disambiguationData":[OSD([sQuery(id+"F13.wireOp",EDGE,"E26.bottom"),sQuery(id+"F13.wireOp",EDGE,"E26.top"),sQuery(id+"F13.wireOp",EDGE,"E26.right"),sQuery(id+"F13.wireOp",EDGE,"E27.bottom"),sQuery(id+"F13.wireOp",EDGE,"E27.top"),sQuery(id+"F13.wireOp",EDGE,"E27.right")])],"isStart":false}),makeQuery(id+"F19.opExtrude","SWEPT_FACE",FACE,{"disambiguationData":[OSD([sQuery(id+"F14.wireOp",EDGE,"E31")])]})]});
            var Q22;
            {var subQ0=sQuery(id+"F4.wireOp",EDGE,"E19.left");var subQ1=sQuery(id+"F4.wireOp",EDGE,"E19.top");var subQ2=sQuery(id+"F4.wireOp",EDGE,"E19.right");var subQ3=sQuery(id+"F4.wireOp",EDGE,"E13");Q22=makeQuery(id+"F17.boolean.opBoolean","INTERSECT",EDGE,{"disambiguationData":[OD(1.0)],"derivedFrom":[makeQuery(id+"F8.boolean.opBoolean","SPLIT",FACE,{"disambiguationData":[TD([makeQuery(id+"F5.opExtrude","SWEPT_FACE",FACE,{"disambiguationData":[OSD([subQ3])]})])],"derivedFrom":makeQuery(id+"F6.boolean.opBoolean","COPY",FACE,{"derivedFrom":makeQuery(id+"F6.opExtrude","CAP_FACE",FACE,{"disambiguationData":[OSD([subQ3,subQ1,subQ0,subQ2])],"isStart":true})})}),makeQuery(id+"F17.opExtrude","SWEPT_FACE",FACE,{"disambiguationData":[OSD([sQuery(id+"F14.wireOp",EDGE,"E31")])]})]});}
            var Q23;
            {var subQ0=sQuery(id+"F4.wireOp",EDGE,"E19.left");var subQ1=sQuery(id+"F4.wireOp",EDGE,"E19.top");var subQ2=sQuery(id+"F4.wireOp",EDGE,"E19.right");var subQ3=sQuery(id+"F4.wireOp",EDGE,"E13");Q23=makeQuery(id+"F17.boolean.opBoolean","INTERSECT",EDGE,{"disambiguationData":[OD(0.0)],"derivedFrom":[makeQuery(id+"F8.boolean.opBoolean","SPLIT",FACE,{"disambiguationData":[TD([makeQuery(id+"F5.opExtrude","SWEPT_FACE",FACE,{"disambiguationData":[OSD([subQ3])]})])],"derivedFrom":makeQuery(id+"F6.boolean.opBoolean","COPY",FACE,{"derivedFrom":makeQuery(id+"F6.opExtrude","CAP_FACE",FACE,{"disambiguationData":[OSD([subQ3,subQ1,subQ0,subQ2])],"isStart":true})})}),makeQuery(id+"F17.opExtrude","SWEPT_FACE",FACE,{"disambiguationData":[OSD([sQuery(id+"F14.wireOp",EDGE,"E31")])]})]});}
            var Q24;
            {var subQ0=sQuery(id+"F4.wireOp",EDGE,"E19.top");var subQ1=sQuery(id+"F4.wireOp",EDGE,"E19.left");Q24=makeQuery(id+"F17.boolean.opBoolean","SPLIT",EDGE,{"disambiguationData":[TD([makeQuery(id+"F5.opExtrude","SWEPT_FACE",FACE,{"disambiguationData":[OSD([subQ0])]})])],"derivedFrom":makeQuery(id+"F6.boolean.opBoolean","COPY",EDGE,{"derivedFrom":makeQuery(id+"F6.opExtrude","CAP_EDGE",EDGE,{"disambiguationData":[OSD([subQ1])],"isStart":true})})});}
            chamfer(context, id + "F25", {"entities" : qUnion([Q0, Q1, Q2, Q3, Q4, Q5, Q6, Q7, Q8, Q9, Q10, Q11, Q12, Q13, Q14, Q15, Q16, Q17, Q18, Q19, Q20, Q21, Q22, Q23, Q24]), "width" : 2 * mm, "tangentPropagation" : true});
        }
        {
            var Q0;
            Q0=makeQuery(id+"F15.opExtrude","SWEPT_FACE",FACE,{"disambiguationData":[OSD([sQuery(id+"F13.wireOp",EDGE,"E27.right")])]});
            var sketch = newSketch(context, id + "F26", { "sketchPlane" : qUnion([Q0])});
            skLineSegment(sketch, "E42.bottom", {"start": v(27, -153) * mm, "end": v(-27, -153) * mm});
            skLineSegment(sketch, "E42.top", {"start": v(27, -225) * mm, "end": v(-27, -225) * mm});
            skLineSegment(sketch, "E42.left", {"start": v(27, -153) * mm, "end": v(27, -225) * mm});
            skLineSegment(sketch, "E42.right", {"start": v(-27, -153) * mm, "end": v(-27, -225) * mm});
            skPoint(sketch, "E42.middle", {"position": v(0, -189) * mm});
            skSolve(sketch);
        }
        {
            var Q0;
            Q0=qSketchRegion(id+"F26",true);
            extrude(context, id + "F27", {"entities" : qUnion([Q0]), "operationType" : NewBodyOperationType.REMOVE, "oppositeDirection" : true, "depth" : 25 * mm});
        }
        {
            var Q0;
            Q0=makeQuery(id+"F15.opExtrude","SWEPT_EDGE",EDGE,{"disambiguationData":[OSD([sQuery(id+"F13.wireOp",EDGE,"E26.bottom"),sQuery(id+"F13.wireOp",EDGE,"E26.right")])]});
            var Q1;
            Q1=makeQuery(id+"F15.opExtrude","SWEPT_EDGE",EDGE,{"disambiguationData":[OSD([sQuery(id+"F13.wireOp",EDGE,"E27.bottom"),sQuery(id+"F13.wireOp",EDGE,"E27.right")])]});
            var Q2;
            Q2=makeQuery(id+"F23.boolean.opBoolean","COPY",EDGE,{"derivedFrom":makeQuery(id+"F23.opExtrude","SWEPT_EDGE",EDGE,{"disambiguationData":[OSD([sQuery(id+"F21.wireOp",EDGE,"E36"),sQuery(id+"F22.wireOp",EDGE,"E41")])]})});
            var Q3;
            Q3=makeQuery(id+"F23.boolean.opBoolean","INTERSECT",EDGE,{"derivedFrom":[makeQuery(id+"F15.opExtrude","SWEPT_FACE",FACE,{"disambiguationData":[OSD([sQuery(id+"F13.wireOp",EDGE,"E26.right")])]}),makeQuery(id+"F23.opExtrude","SWEPT_FACE",FACE,{"disambiguationData":[OSD([sQuery(id+"F21.wireOp",EDGE,"E36")])]})]});
            var Q4;
            Q4=makeQuery(id+"F23.boolean.opBoolean","INTERSECT",EDGE,{"derivedFrom":[makeQuery(id+"F15.opExtrude","SWEPT_FACE",FACE,{"disambiguationData":[OSD([sQuery(id+"F13.wireOp",EDGE,"E26.right")])]}),makeQuery(id+"F23.opExtrude","CAP_FACE",FACE,{"disambiguationData":[OSD([sQuery(id+"F21.wireOp",EDGE,"E36"),sQuery(id+"F22.wireOp",EDGE,"E39.bottom"),sQuery(id+"F22.wireOp",EDGE,"E39.left"),sQuery(id+"F22.wireOp",EDGE,"E41")])],"isStart":true})]});
            var Q5;
            Q5=makeQuery(id+"F23.boolean.opBoolean","COPY",FACE,{"derivedFrom":makeQuery(id+"F23.opExtrude","SWEPT_FACE",FACE,{"disambiguationData":[OSD([sQuery(id+"F22.wireOp",EDGE,"E41")])]})});
            var Q6;
            Q6=makeQuery(id+"F23.boolean.opBoolean","INTERSECT",EDGE,{"derivedFrom":[makeQuery(id+"F15.opExtrude","SWEPT_FACE",FACE,{"disambiguationData":[OSD([sQuery(id+"F13.wireOp",EDGE,"E26.bottom"),sQuery(id+"F13.wireOp",EDGE,"E27.bottom")])]}),makeQuery(id+"F23.opExtrude","CAP_FACE",FACE,{"disambiguationData":[OSD([sQuery(id+"F21.wireOp",EDGE,"E36"),sQuery(id+"F22.wireOp",EDGE,"E39.bottom"),sQuery(id+"F22.wireOp",EDGE,"E39.left"),sQuery(id+"F22.wireOp",EDGE,"E41")])],"isStart":false})]});
            var Q7;
            Q7=makeQuery(id+"F23.boolean.opBoolean","INTERSECT",EDGE,{"derivedFrom":[makeQuery(id+"F15.opExtrude","SWEPT_FACE",FACE,{"disambiguationData":[OSD([sQuery(id+"F13.wireOp",EDGE,"E26.bottom"),sQuery(id+"F13.wireOp",EDGE,"E27.bottom")])]}),makeQuery(id+"F23.opExtrude","CAP_FACE",FACE,{"disambiguationData":[OSD([sQuery(id+"F21.wireOp",EDGE,"E36"),sQuery(id+"F22.wireOp",EDGE,"E39.bottom"),sQuery(id+"F22.wireOp",EDGE,"E39.left"),sQuery(id+"F22.wireOp",EDGE,"E41")])],"isStart":true})]});
            var Q8;
            Q8=makeQuery(id+"F23.boolean.opBoolean","COPY",FACE,{"derivedFrom":makeQuery(id+"F23.opExtrude","SWEPT_FACE",FACE,{"disambiguationData":[OSD([sQuery(id+"F21.wireOp",EDGE,"E36")])]})});
            var Q9;
            Q9=makeQuery(id+"F24.boolean.opBoolean","COPY",FACE,{"derivedFrom":makeQuery(id+"F24.opExtrude","SWEPT_FACE",FACE,{"disambiguationData":[OSD([sQuery(id+"F22.wireOp",EDGE,"E40")])]})});
            var Q10;
            {var subQ0=sQuery(id+"F21.wireOp",EDGE,"E37");var subQ1=makeQuery(id+"F21.imprint","IMPRINT",EDGE,{"derivedFrom":subQ0});Q10=makeQuery(id+"F24.boolean.opBoolean","TWEAK_FACE",FACE,{"derivedFrom":[makeQuery(id+"F24.opExtrude","SWEPT_FACE",FACE,{"disambiguationData":[OSD([subQ0]),TDD([subQ1])]}),makeQuery(id+"F24.opExtrude","SWEPT_FACE",FACE,{"disambiguationData":[OSD([subQ0]),TDD([makeQuery(id+"F22.imprint","IMPRINT",EDGE,{"disambiguationData":[TD([[makeQuery(id+"F22.imprint","INTERSECT",VERTEX,{"disambiguationData":[OD(1.0)],"derivedFrom":[subQ1,sQuery(id+"F22.wireOp",EDGE,"E39.right")]}),1.0]])],"derivedFrom":subQ1})])]})]});}
            var Q11;
            {var subQ0=sQuery(id+"F21.wireOp",EDGE,"E37");Q11=makeQuery(id+"F24.boolean.opBoolean","TWEAK_FACE",FACE,{"derivedFrom":[makeQuery(id+"F24.opExtrude","CAP_FACE",FACE,{"disambiguationData":[OSD([subQ0])],"isStart":false}),makeQuery(id+"F24.opExtrude","CAP_FACE",FACE,{"disambiguationData":[OSD([subQ0,sQuery(id+"F22.wireOp",EDGE,"E39.bottom"),sQuery(id+"F22.wireOp",EDGE,"E39.right"),sQuery(id+"F22.wireOp",EDGE,"E40"),sQuery(id+"F22.wireOp",EDGE,"E41")])],"isStart":false})]});}
            var Q12;
            {var subQ0=sQuery(id+"F21.wireOp",EDGE,"E37");Q12=makeQuery(id+"F24.boolean.opBoolean","TWEAK_FACE",FACE,{"derivedFrom":[makeQuery(id+"F24.opExtrude","CAP_FACE",FACE,{"disambiguationData":[OSD([subQ0])],"isStart":true}),makeQuery(id+"F24.opExtrude","CAP_FACE",FACE,{"disambiguationData":[OSD([subQ0,sQuery(id+"F22.wireOp",EDGE,"E39.bottom"),sQuery(id+"F22.wireOp",EDGE,"E39.right"),sQuery(id+"F22.wireOp",EDGE,"E40"),sQuery(id+"F22.wireOp",EDGE,"E41")])],"isStart":true})]});}
            var Q13;
            Q13=makeQuery(id+"F27.boolean.opBoolean","INTERSECT",EDGE,{"derivedFrom":[makeQuery(id+"F15.opExtrude","SWEPT_FACE",FACE,{"disambiguationData":[OSD([sQuery(id+"F13.wireOp",EDGE,"E26.right")])]}),makeQuery(id+"F27.opExtrude","SWEPT_FACE",FACE,{"disambiguationData":[OSD([sQuery(id+"F26.wireOp",EDGE,"E42.left")])]})]});
            var Q14;
            Q14=makeQuery(id+"F27.boolean.opBoolean","INTERSECT",EDGE,{"derivedFrom":[makeQuery(id+"F15.opExtrude","SWEPT_FACE",FACE,{"disambiguationData":[OSD([sQuery(id+"F13.wireOp",EDGE,"E26.top"),sQuery(id+"F13.wireOp",EDGE,"E27.top")])]}),makeQuery(id+"F27.opExtrude","SWEPT_FACE",FACE,{"disambiguationData":[OSD([sQuery(id+"F26.wireOp",EDGE,"E42.left")])]})]});
            var Q15;
            Q15=makeQuery(id+"F27.boolean.opBoolean","INTERSECT",EDGE,{"derivedFrom":[makeQuery(id+"F15.opExtrude","SWEPT_FACE",FACE,{"disambiguationData":[OSD([sQuery(id+"F13.wireOp",EDGE,"E26.right")])]}),makeQuery(id+"F27.opExtrude","SWEPT_FACE",FACE,{"disambiguationData":[OSD([sQuery(id+"F26.wireOp",EDGE,"E42.bottom")])]})]});
            var Q16;
            Q16=makeQuery(id+"F27.boolean.opBoolean","COPY",EDGE,{"derivedFrom":makeQuery(id+"F27.opExtrude","CAP_EDGE",EDGE,{"disambiguationData":[OSD([sQuery(id+"F26.wireOp",EDGE,"E42.bottom")])],"isStart":true})});
            var Q17;
            Q17=makeQuery(id+"F27.boolean.opBoolean","COPY",EDGE,{"derivedFrom":makeQuery(id+"F27.opExtrude","CAP_EDGE",EDGE,{"disambiguationData":[OSD([sQuery(id+"F26.wireOp",EDGE,"E42.left")])],"isStart":true})});
            var Q18;
            Q18=makeQuery(id+"F27.boolean.opBoolean","INTERSECT",EDGE,{"derivedFrom":[makeQuery(id+"F15.opExtrude","SWEPT_FACE",FACE,{"disambiguationData":[OSD([sQuery(id+"F13.wireOp",EDGE,"E26.right")])]}),makeQuery(id+"F27.opExtrude","SWEPT_FACE",FACE,{"disambiguationData":[OSD([sQuery(id+"F26.wireOp",EDGE,"E42.right")])]})]});
            var Q19;
            Q19=makeQuery(id+"F27.boolean.opBoolean","COPY",EDGE,{"derivedFrom":makeQuery(id+"F27.opExtrude","CAP_EDGE",EDGE,{"disambiguationData":[OSD([sQuery(id+"F26.wireOp",EDGE,"E42.right")])],"isStart":true})});
            chamfer(context, id + "F28", {"entities" : qUnion([Q0, Q1, Q2, Q3, Q4, Q5, Q6, Q7, Q8, Q9, Q10, Q11, Q12, Q13, Q14, Q15, Q16, Q17, Q18, Q19]), "width" : .5 * mm, "tangentPropagation" : true});
        }
    });
